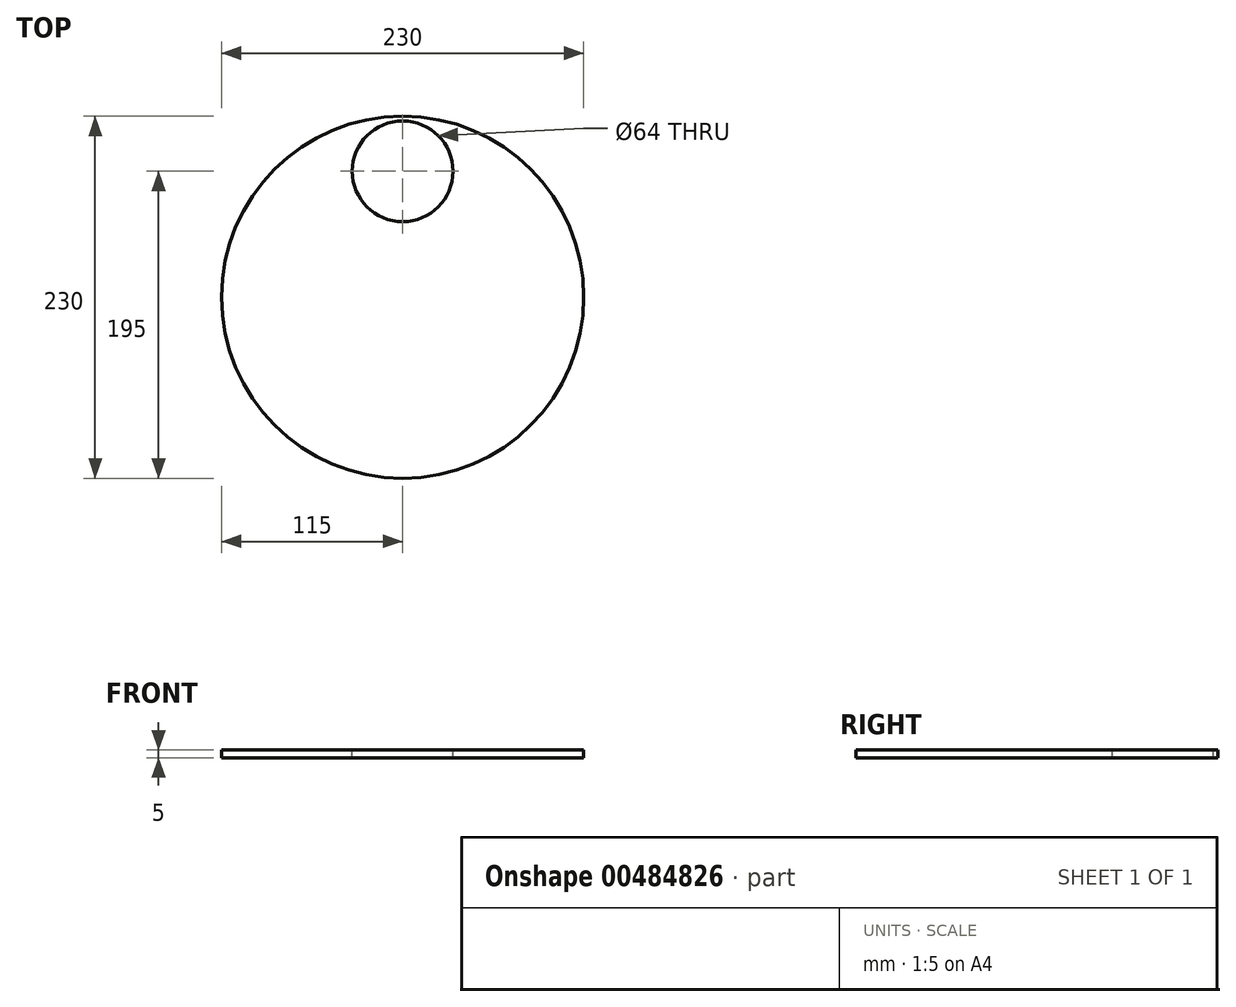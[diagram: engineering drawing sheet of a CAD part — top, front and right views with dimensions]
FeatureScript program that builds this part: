
annotation { "Feature Type Name" : "Feature", "Feature Type Description" : "" }
export const myFeature = defineFeature(function(context is Context, id is Id, definition is map)
    precondition{}
    {
        {
            var Q0;
            Q0=qCreatedBy(makeId("Top.planeOp"),FACE);
            var sketch = newSketch(context, id + "F0", { "sketchPlane" : qUnion([Q0])});
            skCircle(sketch, "E0", {"center": v(0, 0) * mm, "radius": 115 * mm});
            skSolve(sketch);
        }
        {
            var Q0;
            Q0 = qSketchRegion(id + "F0", true);
            extrude(context, id + "F1", {"entities" : qUnion([Q0]), "depth" : 5 * mm});
        }
        {
            var Q0;
            Q0=makeQuery(id+"F1.opExtrude","CAP_FACE",FACE,{"disambiguationData":[OSD([sQuery(id+"F0.wireOp",EDGE,"E0")])],"isStart":false});
            var sketch = newSketch(context, id + "F2", { "sketchPlane" : qUnion([Q0])});
            skLineSegment(sketch, "E1", {"start": v(0, 0) * mm, "end": v(0, 80) * mm, "construction": true});
            skCircle(sketch, "E2", {"center": v(0, 80) * mm, "radius": 32 * mm});
            skSolve(sketch);
        }
        {
            var Q0;
            Q0=makeQuery(id+"F2.imprint","IMPRINT",FACE,{"disambiguationData":[TD([[makeQuery(id+"F2.imprint","IMPRINT",EDGE,{"derivedFrom":sQuery(id+"F2.wireOp",EDGE,"E2")}),1.0]])]});
            var Q1;
            Q1=sQuery(id+"F2.wireOp",EDGE,"E2");
            extrude(context, id + "F3", {"entities" : qUnion([Q0]), "operationType" : NewBodyOperationType.REMOVE, "surfaceEntities" : qUnion([Q1]), "oppositeDirection" : true, "depth" : 5 * mm});
        }
    });
